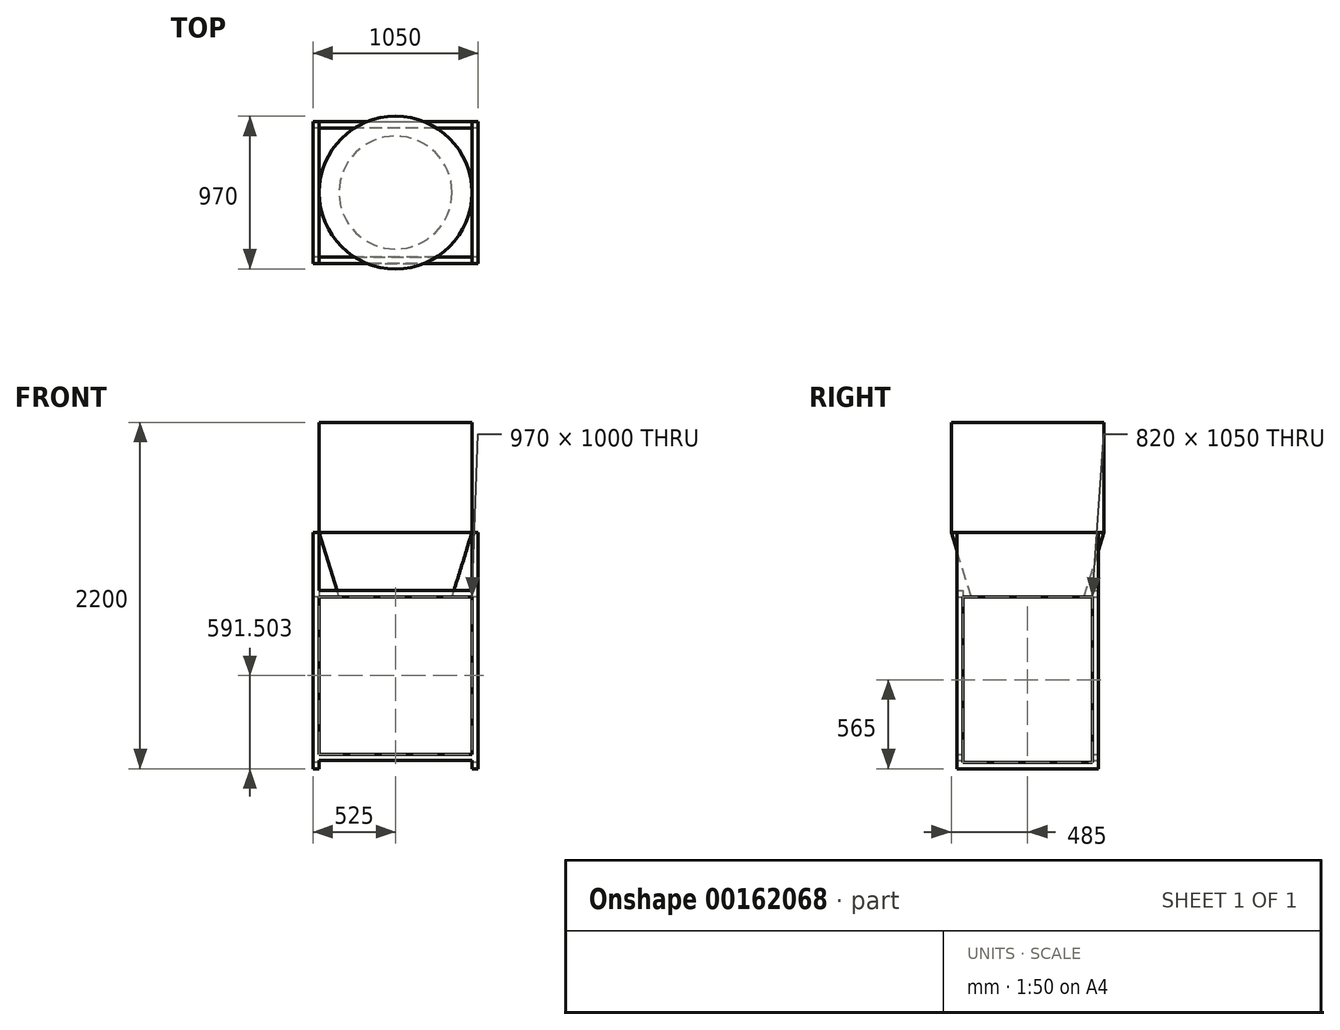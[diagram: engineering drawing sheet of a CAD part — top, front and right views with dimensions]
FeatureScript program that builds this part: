
annotation { "Feature Type Name" : "Feature", "Feature Type Description" : "" }
export const myFeature = defineFeature(function(context is Context, id is Id, definition is map)
    precondition{}
    {
        {
            var Q0;
            Q0=qCreatedBy(makeId("Front.planeOp"),FACE);
            var sketch = newSketch(context, id + "F0", { "sketchPlane" : qUnion([Q0])});
            skLineSegment(sketch, "E0", {"start": v(0, 0) * mm, "end": v(0, 1500) * mm});
            skLineSegment(sketch, "E1", {"start": v(0, 1500) * mm, "end": v(40, 1500) * mm});
            skLineSegment(sketch, "E2", {"start": v(40, 1500) * mm, "end": v(40, 1131.5) * mm});
            skLineSegment(sketch, "E3", {"start": v(40, 1131.5) * mm, "end": v(1010, 1131.5) * mm});
            skLineSegment(sketch, "E4", {"start": v(1010, 1131.5) * mm, "end": v(1010, 1500) * mm});
            skLineSegment(sketch, "E5", {"start": v(1010, 1500) * mm, "end": v(1050, 1500) * mm});
            skLineSegment(sketch, "E6", {"start": v(1050, 1500) * mm, "end": v(1050, 0) * mm});
            skLineSegment(sketch, "E7", {"start": v(1050, 0) * mm, "end": v(1010, 0) * mm});
            skLineSegment(sketch, "E8", {"start": v(1010, 0) * mm, "end": v(1010, 51.5) * mm});
            skLineSegment(sketch, "E9", {"start": v(1010, 51.5) * mm, "end": v(40, 51.5) * mm});
            skLineSegment(sketch, "E10", {"start": v(40, 51.5) * mm, "end": v(40, 0) * mm});
            skLineSegment(sketch, "E11", {"start": v(40, 0) * mm, "end": v(0, 0) * mm});
            skLineSegment(sketch, "E12.bottom", {"start": v(40, 1091.5) * mm, "end": v(1010, 1091.5) * mm});
            skLineSegment(sketch, "E12.top", {"start": v(40, 91.5) * mm, "end": v(1010, 91.5) * mm});
            skLineSegment(sketch, "E12.left", {"start": v(40, 1091.5) * mm, "end": v(40, 91.5) * mm});
            skLineSegment(sketch, "E12.right", {"start": v(1010, 1091.5) * mm, "end": v(1010, 91.5) * mm});
            skSolve(sketch);
        }
        {
            var Q0;
            Q0 = qSketchRegion(id + "F0", true);
            extrude(context, id + "F1", {"entities" : qUnion([Q0]), "depth" : 900 * mm});
        }
        {
            var Q0;
            Q0=makeQuery(id+"F1.opExtrude","SWEPT_FACE",FACE,{"disambiguationData":[OSD([sQuery(id+"F0.wireOp",EDGE,"E9")])]});
            var sketch = newSketch(context, id + "F2", { "sketchPlane" : qUnion([Q0])});
            skLineSegment(sketch, "E13.bottom", {"start": v(40, 860) * mm, "end": v(1010, 860) * mm});
            skLineSegment(sketch, "E13.top", {"start": v(40, 40) * mm, "end": v(1010, 40) * mm});
            skLineSegment(sketch, "E13.left", {"start": v(40, 860) * mm, "end": v(40, 40) * mm});
            skLineSegment(sketch, "E13.right", {"start": v(1010, 860) * mm, "end": v(1010, 40) * mm});
            skSolve(sketch);
        }
        {
            var Q0;
            Q0 = qSketchRegion(id + "F2", true);
            extrude(context, id + "F3", {"entities" : qUnion([Q0]), "operationType" : NewBodyOperationType.REMOVE, "endBound" : BoundingType.THROUGH_ALL, "oppositeDirection" : true, "depth" : 25 * mm});
        }
        {
            var Q0;
            Q0=makeQuery(id+"F1.opExtrude","SWEPT_FACE",FACE,{"disambiguationData":[OSD([sQuery(id+"F0.wireOp",EDGE,"E1")])]});
            var sketch = newSketch(context, id + "F4", { "sketchPlane" : qUnion([Q0])});
            skCircle(sketch, "E14", {"center": v(525, -450) * mm, "radius": 485 * mm});
            skSolve(sketch);
        }
        {
            var Q0;
            Q0 = qSketchRegion(id + "F4", true);
            extrude(context, id + "F5", {"entities" : qUnion([Q0]), "operationType" : NewBodyOperationType.ADD, "depth" : 700 * mm});
        }
        {
            var Q0;
            Q0=makeQuery(id+"F1.opExtrude","CAP_FACE",FACE,{"disambiguationData":[OSD([sQuery(id+"F0.wireOp",EDGE,"E0"),sQuery(id+"F0.wireOp",EDGE,"E1"),sQuery(id+"F0.wireOp",EDGE,"E2"),sQuery(id+"F0.wireOp",EDGE,"E3"),sQuery(id+"F0.wireOp",EDGE,"E4"),sQuery(id+"F0.wireOp",EDGE,"E5"),sQuery(id+"F0.wireOp",EDGE,"E6"),sQuery(id+"F0.wireOp",EDGE,"E7"),sQuery(id+"F0.wireOp",EDGE,"E8"),sQuery(id+"F0.wireOp",EDGE,"E9"),sQuery(id+"F0.wireOp",EDGE,"E10"),sQuery(id+"F0.wireOp",EDGE,"E11"),sQuery(id+"F0.wireOp",EDGE,"E12.bottom"),sQuery(id+"F0.wireOp",EDGE,"E12.top"),sQuery(id+"F0.wireOp",EDGE,"E12.left"),sQuery(id+"F0.wireOp",EDGE,"E12.right")])],"isStart":false});
            cPlane(context, id + "F6", {"entities" : qUnion([Q0]), "cplaneType" : CPlaneType.OFFSET, "offset" : 450 * mm, "oppositeDirection" : true, "width" : 150 * mm, "height" : 150 * mm});
        }
        {
            var Q0;
            Q0=qCreatedBy(id+"F6.planeOp",FACE);
            var sketch = newSketch(context, id + "F7", { "sketchPlane" : qUnion([Q0])});
            skLineSegment(sketch, "E15", {"start": v(525, 1500) * mm, "end": v(525, 900) * mm});
            skLineSegment(sketch, "E16", {"start": v(525, 900) * mm, "end": v(225, 900) * mm});
            skLineSegment(sketch, "E17", {"start": v(225, 900) * mm, "end": v(40, 1500) * mm});
            skLineSegment(sketch, "E18", {"start": v(40, 1500) * mm, "end": v(525, 1500) * mm});
            skSolve(sketch);
        }
        {
            var Q0;
            Q0 = qSketchRegion(id + "F7", true);
            var Q1;
            Q1=sQuery(id+"F7.wireOp",EDGE,"E15");
            revolve(context, id + "F8", {"entities" : qUnion([Q0]), "axis" : qUnion([Q1]), "revolveType" : RevolveType.FULL});
        }
        {
            var Q0;
            Q0=makeQuery(id+"F1.opExtrude","SWEPT_FACE",FACE,{"disambiguationData":[OSD([sQuery(id+"F0.wireOp",EDGE,"E0")])]});
            var sketch = newSketch(context, id + "F9", { "sketchPlane" : qUnion([Q0])});
            skLineSegment(sketch, "E19.bottom", {"start": v(860, 1090) * mm, "end": v(40, 1090) * mm});
            skLineSegment(sketch, "E19.top", {"start": v(860, 40) * mm, "end": v(40, 40) * mm});
            skLineSegment(sketch, "E19.left", {"start": v(860, 1090) * mm, "end": v(860, 40) * mm});
            skLineSegment(sketch, "E19.right", {"start": v(40, 1090) * mm, "end": v(40, 40) * mm});
            skSolve(sketch);
        }
        {
            var Q0;
            Q0 = qSketchRegion(id + "F9", true);
            extrude(context, id + "F10", {"entities" : qUnion([Q0]), "operationType" : NewBodyOperationType.REMOVE, "endBound" : BoundingType.THROUGH_ALL, "oppositeDirection" : true, "depth" : 25 * mm});
        }
    });
